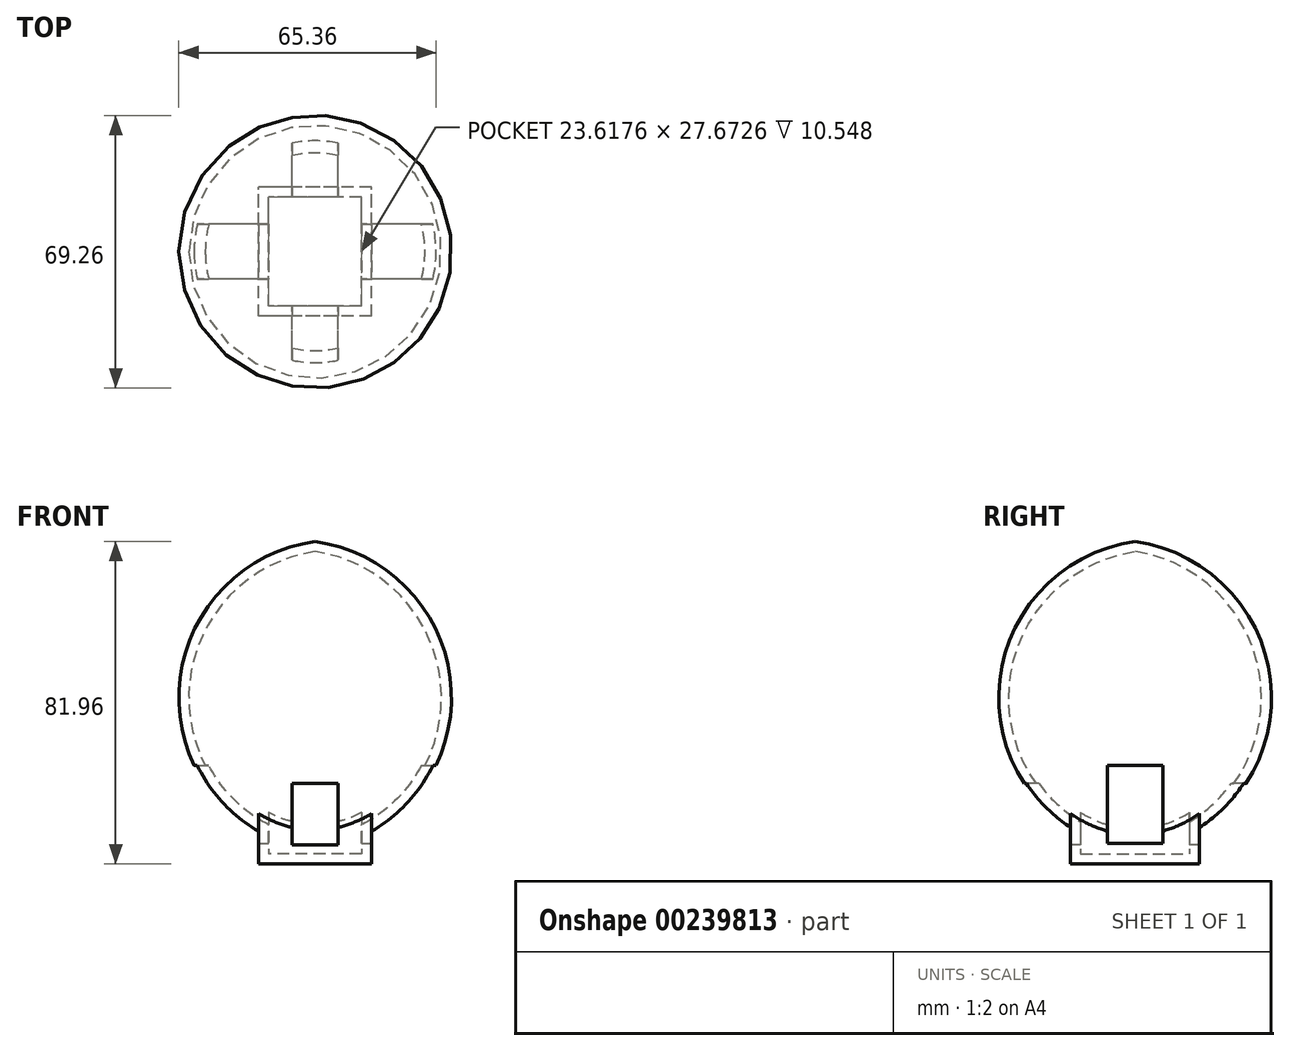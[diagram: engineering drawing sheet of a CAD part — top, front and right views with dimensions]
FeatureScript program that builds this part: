
annotation { "Feature Type Name" : "Feature", "Feature Type Description" : "" }
export const myFeature = defineFeature(function(context is Context, id is Id, definition is map)
    precondition{}
    {
        {
            var Q0;
            Q0=qCreatedBy(makeId("Front.planeOp"),FACE);
            var sketch = newSketch(context, id + "F0", { "sketchPlane" : qUnion([Q0])});
            skArc(sketch, "E0", {"start": v(0, 79.42) * mm, "mid": v(-34.63, 39.7) * mm, "end": v(0, 0) * mm});
            skLineSegment(sketch, "E1", {"start": v(0, 79.42) * mm, "end": v(0, 0) * mm});
            skSolve(sketch);
        }
        {
            var Q0;
            Q0 = qSketchRegion(id + "F0", true);
            var Q1;
            Q1=sQuery(id+"F0.wireOp",EDGE,"E1");
            revolve(context, id + "F1", {"entities" : qUnion([Q0]), "axis" : qUnion([Q1]), "revolveType" : RevolveType.FULL});
        }
        {
            var Q0;
            Q0=qCreatedBy(makeId("Top.planeOp"),FACE);
            var sketch = newSketch(context, id + "F2", { "sketchPlane" : qUnion([Q0])});
            skLineSegment(sketch, "E2.bottom", {"start": v(14.35, -16.38) * mm, "end": v(-14.35, -16.38) * mm});
            skLineSegment(sketch, "E2.top", {"start": v(14.35, 16.38) * mm, "end": v(-14.35, 16.38) * mm});
            skLineSegment(sketch, "E2.left", {"start": v(14.35, -16.38) * mm, "end": v(14.35, 16.38) * mm});
            skLineSegment(sketch, "E2.right", {"start": v(-14.35, -16.38) * mm, "end": v(-14.35, 16.38) * mm});
            skPoint(sketch, "E2.middle", {"position": v(0, 0) * mm});
            skSolve(sketch);
        }
        {
            var Q0;
            Q0 = qSketchRegion(id + "F2", true);
            extrude(context, id + "F3", {"entities" : qUnion([Q0]), "operationType" : NewBodyOperationType.ADD, "depth" : 25.4 * mm});
        }
        {
            var Q0;
            Q0=makeQuery(id+"F3.opExtrude","CAP_FACE",FACE,{"disambiguationData":[OSD([sQuery(id+"F2.wireOp",EDGE,"E2.bottom"),sQuery(id+"F2.wireOp",EDGE,"E2.top"),sQuery(id+"F2.wireOp",EDGE,"E2.left"),sQuery(id+"F2.wireOp",EDGE,"E2.right")])],"isStart":true});
            shell(context, id + "F4", {"entities" : qUnion([Q0]), "thickness" : 2.54 * mm});
        }
        {
            var Q0;
            Q0=makeQuery(id+"F3.opExtrude","CAP_FACE",FACE,{"disambiguationData":[OSD([sQuery(id+"F2.wireOp",EDGE,"E2.bottom"),sQuery(id+"F2.wireOp",EDGE,"E2.top"),sQuery(id+"F2.wireOp",EDGE,"E2.left"),sQuery(id+"F2.wireOp",EDGE,"E2.right")])],"isStart":true});
            var sketch = newSketch(context, id + "F5", { "sketchPlane" : qUnion([Q0])});
            skLineSegment(sketch, "E3.0", {"start": v(14.35, 16.38) * mm, "end": v(-14.35, 16.38) * mm});
            skLineSegment(sketch, "E3.1", {"start": v(-14.35, 16.38) * mm, "end": v(-14.35, -16.38) * mm});
            skLineSegment(sketch, "E3.2", {"start": v(14.35, -16.38) * mm, "end": v(-14.35, -16.38) * mm});
            skLineSegment(sketch, "E3.3", {"start": v(14.35, 16.38) * mm, "end": v(14.35, -16.38) * mm});
            skSolve(sketch);
        }
        {
            var Q0;
            Q0 = qSketchRegion(id + "F5", true);
            extrude(context, id + "F6", {"entities" : qUnion([Q0]), "operationType" : NewBodyOperationType.ADD, "depth" : 2.54 * mm});
        }
        {
            var Q0;
            Q0=qCreatedBy(makeId("Front.planeOp"),FACE);
            var sketch = newSketch(context, id + "F7", { "sketchPlane" : qUnion([Q0])});
            skLineSegment(sketch, "E4.bottom", {"start": v(5.83, 17.9) * mm, "end": v(-5.83, 17.9) * mm});
            skLineSegment(sketch, "E4.top", {"start": v(5.83, 2.3) * mm, "end": v(-5.83, 2.3) * mm});
            skLineSegment(sketch, "E4.left", {"start": v(5.83, 17.9) * mm, "end": v(5.83, 2.3) * mm});
            skLineSegment(sketch, "E4.right", {"start": v(-5.83, 17.9) * mm, "end": v(-5.83, 2.3) * mm});
            skPoint(sketch, "E4.middle", {"position": v(0, 10.1) * mm});
            skSolve(sketch);
        }
        {
            var Q0;
            Q0 = qSketchRegion(id + "F7", true);
            extrude(context, id + "F8", {"entities" : qUnion([Q0]), "operationType" : NewBodyOperationType.REMOVE, "endBound" : BoundingType.SYMMETRIC, "oppositeDirection" : true, "depth" : 138.18 * mm});
        }
        {
            var Q0;
            Q0=qCreatedBy(makeId("Right.planeOp"),FACE);
            var sketch = newSketch(context, id + "F9", { "sketchPlane" : qUnion([Q0])});
            skLineSegment(sketch, "E5.bottom", {"start": v(-7, 22.47) * mm, "end": v(7, 22.47) * mm});
            skLineSegment(sketch, "E5.top", {"start": v(-7, 2.72) * mm, "end": v(7, 2.72) * mm});
            skLineSegment(sketch, "E5.left", {"start": v(-7, 22.47) * mm, "end": v(-7, 2.72) * mm});
            skLineSegment(sketch, "E5.right", {"start": v(7, 22.47) * mm, "end": v(7, 2.72) * mm});
            skPoint(sketch, "E5.middle", {"position": v(0, 12.6) * mm});
            skSolve(sketch);
        }
        {
            var Q0;
            Q0 = qSketchRegion(id + "F9", true);
            extrude(context, id + "F10", {"entities" : qUnion([Q0]), "operationType" : NewBodyOperationType.REMOVE, "endBound" : BoundingType.SYMMETRIC, "oppositeDirection" : true, "depth" : 156.97 * mm});
        }
    });
